# Revit family: Genie_Site_ArticulatingBoom_(S-80J)1
name_source: partatom
category: Site
revit_build: Autodesk Revit 2018 (Build: 20190510_1515(x64)
units: mm (PartAtom-declared; Revit-internal decimal feet)

## family parameters
Always vertical = Yes
Cut with Voids When Loaded = No
OmniClass Number = 23.50.85.17
OmniClass Title = Telescoping Platforms
Part Type = Normal
Round Connector Dimension = Use Diameter
Shared = No
Work Plane-Based = No

## types (1)
- S-80J
    Assembly Code = E1030900
    AssetType = Moveable
    BIMObjectName = Genie_Site_ArticulatingBoom_(S-80J)
    ClassificationName = Uniclass2015
    ClassificationValue = Pr_65_80_47_95
    Color = Grey & Blue
    Cost = 0 $
    Description = The Genie S-80 J model has an unre­stricted platform capacity of 660 lb (300 kg) to get the job done with two occupants, plus tools, and a 6-ft (1.8 m) jib, leading length and capacity for low-weight booms in this height category. With a platform height of 80 ft (24.4 m) and horizontal reach of 55 ft (16.8 m), this new boom provides operators with access where it’s needed — at the top of the envelope. This new addition to the Genie essential performance boom line offers rental companies the opportunity to increase their rental return on invested capital (rROIC) by mixing their fleets with a variety of Genie booms, matching the right boom to the right application.
    DocumentationLiterature = https://www.genielift.com
    DocumentationTechnical = https://www.genielift.com
    DurationUnit = Years
    ExpectedLife = 0
    Features = Suited for use in general construction, maintenance, inspection and painting tasks. Leading unrestricted platform capacity of 660 lb (300 kg) with 6-ft (1.8 m) jib. Low 16,650 lb (7550 kg) operating weight in a compact chassis design. Platform height of 60 ft 10 in (18.5 m) and horizontal reach of 40 ft 6 in (12.3 m). 1 ft 10 in (56.4 cm) of ground clearance to clear obstacles.
    Finish = Painted Steel
    IfcExportAs = IfcTransportElement
    IfcExportType = IfcTransportElementType
    Keynote = X
    Manufacturer = Genie
    ManufacturerName = Genie
    Material = Painted Steel
    Model = Genie - Articulating Boom
    ModelNumber = S-80J
    ModelReference = Genie - Articulating Boom
    NBSDescription = Vertical lifting platforms
    NBSObjectName = Genie - Vertical lifting platforms
    NBSReference = 90-80-65/350
    NominalDepth = 2490 mm
    NominalHeight = 2740 mm
    NominalLength = 10440 mm  [stored 34.252 ft]
    ProductionYear = 2020
    Size = 2.49m x 2.74m x 10.44m
    Type Comments = S-80J
    TypeName = Genie - Articulating Boom
    URL = http://www.genielift.co.uk
    WarrantyDurationLabor = 0
    WarrantyDurationParts = 0
    WarrantyDurationUnit = Years
    WarrantyGuarantorLabor = http://www.genielift.co.uk
    WarrantyGuarantorParts = http://www.genielift.co.uk
    _BSBibleVersion = 16
    _BimSpecGuid = 0
    _CurrentRevision = 1
    _DistributedBy = www.bimstore.co

note: [stored X ft] marks values corroborated as IEEE doubles in the binary element streams (Revit-internal decimal feet)

## geometry (parser evidence)
native form markers: Sweep x33
no freeform markers — native parametric forms only
